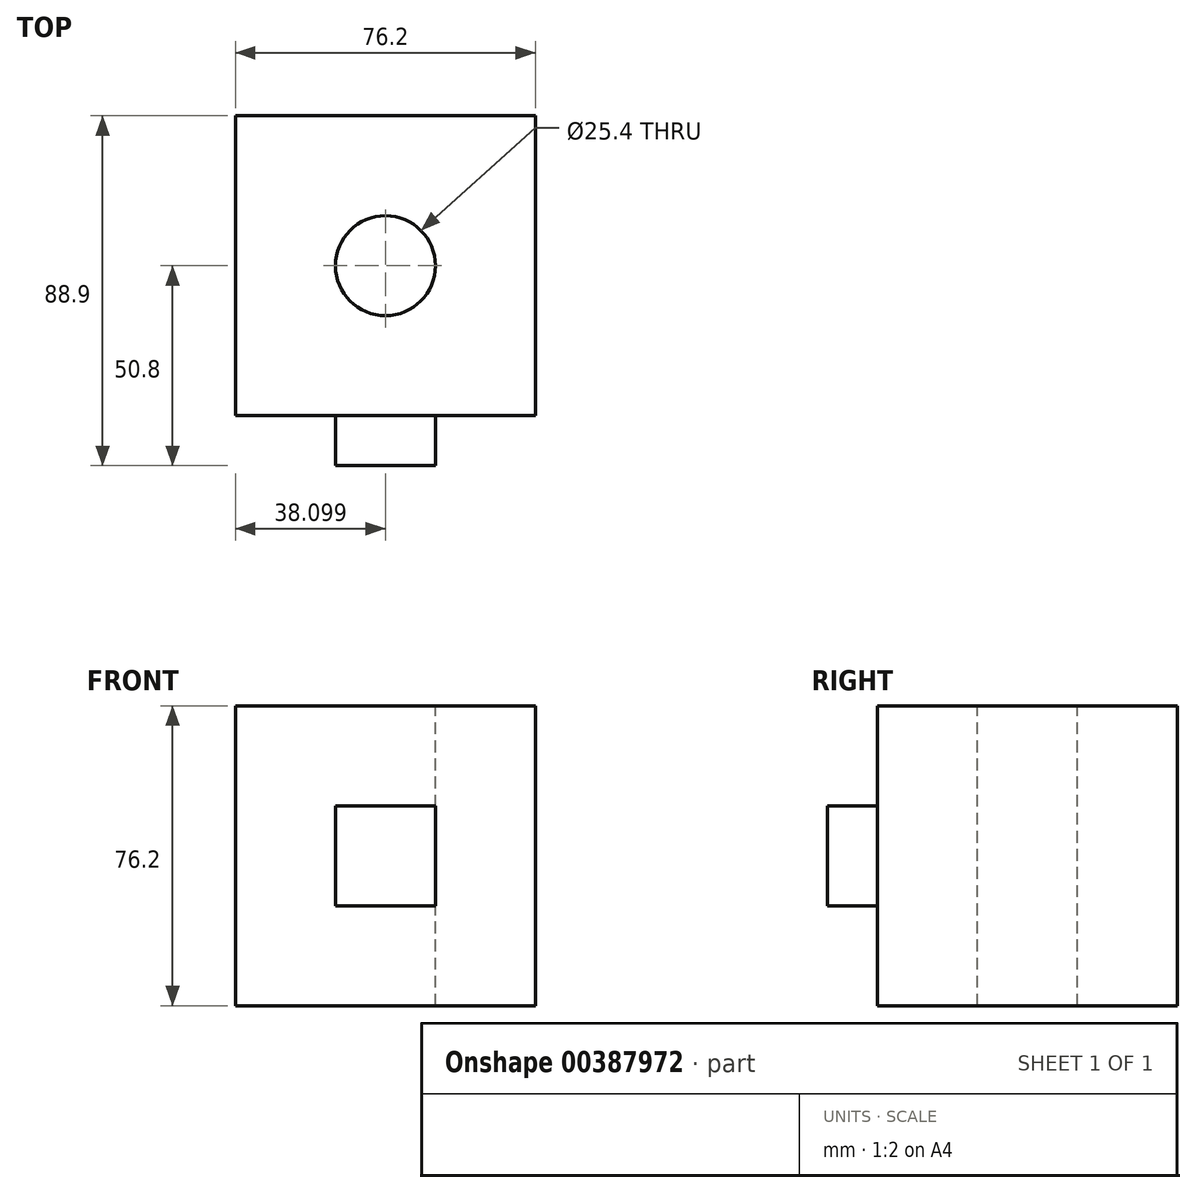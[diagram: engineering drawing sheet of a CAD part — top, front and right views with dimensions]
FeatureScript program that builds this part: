
annotation { "Feature Type Name" : "Feature", "Feature Type Description" : "" }
export const myFeature = defineFeature(function(context is Context, id is Id, definition is map)
    precondition{}
    {
        {
            var Q0;
            Q0=qCreatedBy(makeId("Front.planeOp"),FACE);
            var sketch = newSketch(context, id + "F0", { "sketchPlane" : qUnion([Q0])});
            skLineSegment(sketch, "E0.bottom", {"start": v(-67.72, -31.2) * mm, "end": v(8.48, -31.2) * mm});
            skLineSegment(sketch, "E0.top", {"start": v(-67.72, 45) * mm, "end": v(8.48, 45) * mm});
            skLineSegment(sketch, "E0.left", {"start": v(-67.72, -31.2) * mm, "end": v(-67.72, 45) * mm});
            skLineSegment(sketch, "E0.right", {"start": v(8.48, -31.2) * mm, "end": v(8.48, 45) * mm});
            skSolve(sketch);
        }
        {
            var Q0;
            Q0 = qSketchRegion(id + "F0", true);
            extrude(context, id + "F1", {"entities" : qUnion([Q0]), "depth" : 76.2 * mm});
        }
        {
            var Q0;
            Q0=makeQuery(id+"F1.opExtrude","SWEPT_FACE",FACE,{"disambiguationData":[OSD([sQuery(id+"F0.wireOp",EDGE,"E0.top")])]});
            var sketch = newSketch(context, id + "F2", { "sketchPlane" : qUnion([Q0])});
            skPoint(sketch, "E1", {"position": v(-29.62, -38.1) * mm});
            skSolve(sketch);
        }
        {
            var Q0;
            Q0=sQuery(id+"F2.wireOp",VERTEX,"E1");
            var Q1;
            Q1=makeQuery(id+"F1.opExtrude","SWEPT_BODY",BODY,{"disambiguationData":[OSD([sQuery(id+"F0.wireOp",EDGE,"E0.bottom"),sQuery(id+"F0.wireOp",EDGE,"E0.top"),sQuery(id+"F0.wireOp",EDGE,"E0.left"),sQuery(id+"F0.wireOp",EDGE,"E0.right")])]});
            hole(context, id + "F3", {"style" : HoleStyle.SIMPLE, "endStyle" : HoleEndStyle.THROUGH, "holeDiameter" : 25.4 * mm, "isTappedThrough" : true, "tappedDepth" : 12.7 * mm, "tapClearance" : 3, "locations" : qUnion([Q0]), "scope" : qUnion([Q1])});
        }
        {
            var Q0;
            Q0=makeQuery(id+"F1.opExtrude","CAP_FACE",FACE,{"disambiguationData":[OSD([sQuery(id+"F0.wireOp",EDGE,"E0.bottom"),sQuery(id+"F0.wireOp",EDGE,"E0.top"),sQuery(id+"F0.wireOp",EDGE,"E0.left"),sQuery(id+"F0.wireOp",EDGE,"E0.right")])],"isStart":false});
            var sketch = newSketch(context, id + "F4", { "sketchPlane" : qUnion([Q0])});
            skLineSegment(sketch, "E2.bottom", {"start": v(-42.32, -5.8) * mm, "end": v(-16.92, -5.8) * mm});
            skLineSegment(sketch, "E2.top", {"start": v(-42.32, 19.6) * mm, "end": v(-16.92, 19.6) * mm});
            skLineSegment(sketch, "E2.left", {"start": v(-42.32, -5.8) * mm, "end": v(-42.32, 19.6) * mm});
            skLineSegment(sketch, "E2.right", {"start": v(-16.92, -5.8) * mm, "end": v(-16.92, 19.6) * mm});
            skSolve(sketch);
        }
        {
            var Q0;
            Q0=makeQuery(id+"F4.imprint","IMPRINT",FACE,{"disambiguationData":[TD([[makeQuery(id+"F4.imprint","IMPRINT",EDGE,{"derivedFrom":sQuery(id+"F4.wireOp",EDGE,"E2.bottom")}),1.0]])]});
            extrude(context, id + "F5", {"entities" : qUnion([Q0]), "operationType" : NewBodyOperationType.ADD, "depth" : 12.7 * mm});
        }
    });
